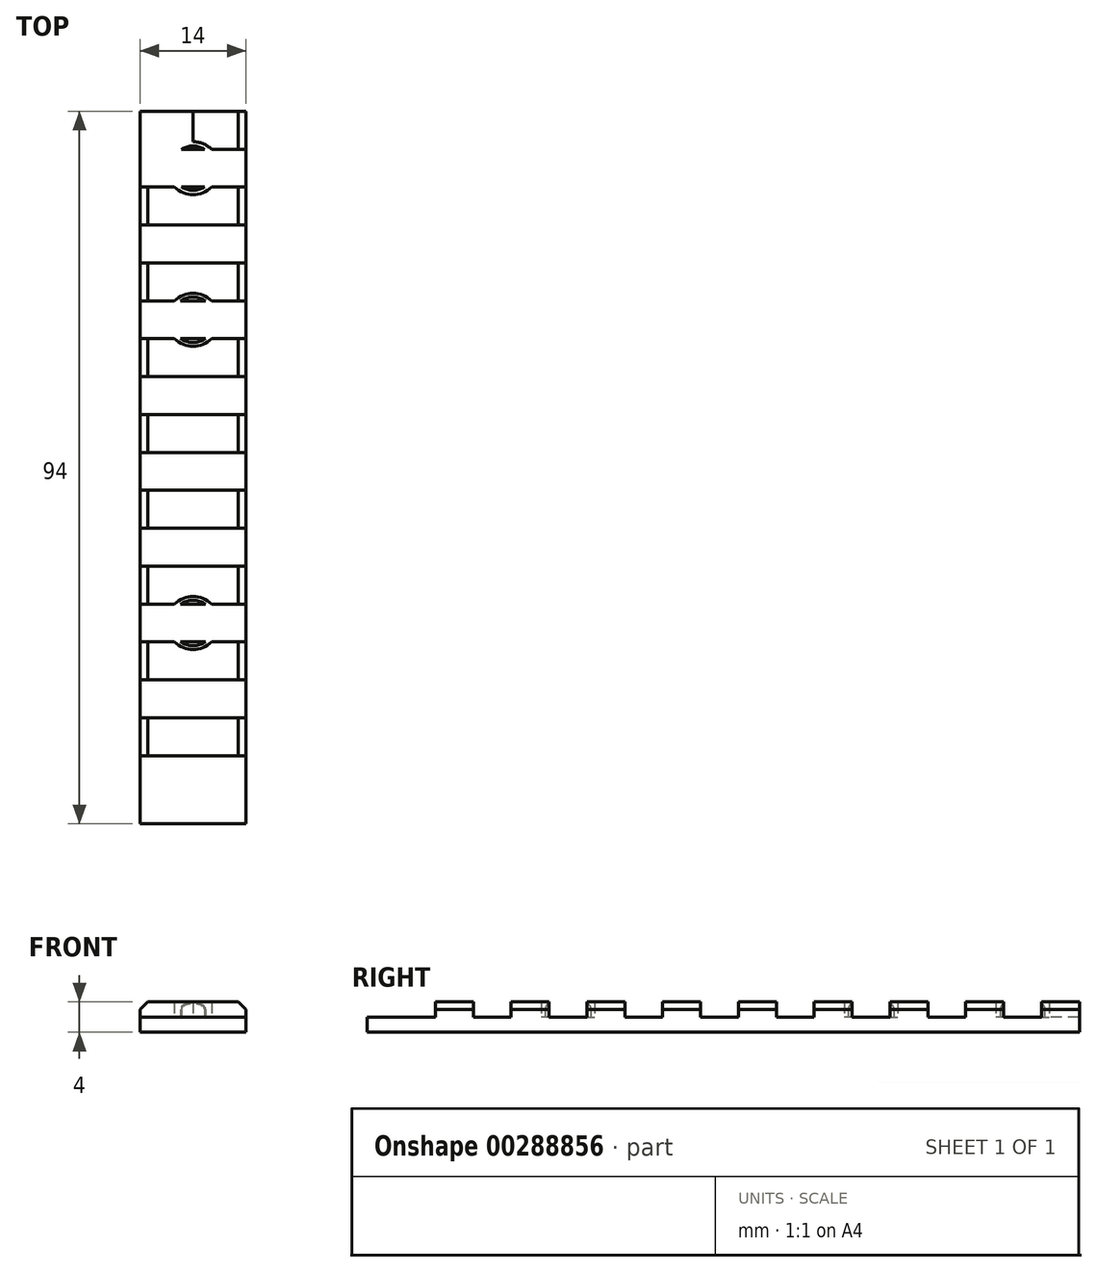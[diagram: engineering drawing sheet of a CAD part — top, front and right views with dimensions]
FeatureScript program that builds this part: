
annotation { "Feature Type Name" : "Feature", "Feature Type Description" : "" }
export const myFeature = defineFeature(function(context is Context, id is Id, definition is map)
    precondition{}
    {
        {
            var Q0;
            Q0=qCreatedBy(makeId("Top.planeOp"),FACE);
            var sketch = newSketch(context, id + "F0", { "sketchPlane" : qUnion([Q0])});
            skLineSegment(sketch, "E0.bottom", {"start": v(-14, 58.07) * mm, "end": v(0, 58.07) * mm});
            skLineSegment(sketch, "E0.top", {"start": v(-14, -35.93) * mm, "end": v(0, -35.93) * mm});
            skLineSegment(sketch, "E0.left", {"start": v(-14, 58.07) * mm, "end": v(-14, -35.93) * mm});
            skLineSegment(sketch, "E0.right", {"start": v(0, 58.07) * mm, "end": v(0, -35.93) * mm});
            skSolve(sketch);
        }
        {
            var Q0;
            Q0 = qSketchRegion(id + "F0", true);
            extrude(context, id + "F1", {"entities" : qUnion([Q0]), "depth" : 2 * mm});
        }
        {
            var Q0;
            Q0=makeQuery(id+"F1.opExtrude","CAP_FACE",FACE,{"disambiguationData":[OSD([sQuery(id+"F0.wireOp",EDGE,"E0.bottom"),sQuery(id+"F0.wireOp",EDGE,"E0.top"),sQuery(id+"F0.wireOp",EDGE,"E0.left"),sQuery(id+"F0.wireOp",EDGE,"E0.right")])],"isStart":false});
            var sketch = newSketch(context, id + "F2", { "sketchPlane" : qUnion([Q0])});
            skLineSegment(sketch, "E1", {"start": v(-14, 58.07) * mm, "end": v(-14, 48.07) * mm});
            skLineSegment(sketch, "E2.bottom", {"start": v(-14, 48.07) * mm, "end": v(0, 48.07) * mm});
            skLineSegment(sketch, "E2.top", {"start": v(-14, 43.07) * mm, "end": v(0, 43.07) * mm});
            skLineSegment(sketch, "E2.left", {"start": v(-14, 48.07) * mm, "end": v(-14, 43.07) * mm});
            skLineSegment(sketch, "E2.right", {"start": v(0, 48.07) * mm, "end": v(0, 43.07) * mm});
            skLineSegment(sketch, "E3", {"start": v(-14, 43.07) * mm, "end": v(-14, 38.07) * mm});
            skLineSegment(sketch, "E4.bottom", {"start": v(-14, 38.07) * mm, "end": v(0, 38.07) * mm});
            skLineSegment(sketch, "E4.top", {"start": v(-14, 33.07) * mm, "end": v(0, 33.07) * mm});
            skLineSegment(sketch, "E4.left", {"start": v(-14, 38.07) * mm, "end": v(-14, 33.07) * mm});
            skLineSegment(sketch, "E4.right", {"start": v(0, 38.07) * mm, "end": v(0, 33.07) * mm});
            skLineSegment(sketch, "E5", {"start": v(-14, 33.07) * mm, "end": v(-14, 28.07) * mm});
            skLineSegment(sketch, "E6.bottom", {"start": v(-14, 28.07) * mm, "end": v(0, 28.07) * mm});
            skLineSegment(sketch, "E6.top", {"start": v(-14, 23.07) * mm, "end": v(0, 23.07) * mm});
            skLineSegment(sketch, "E6.left", {"start": v(-14, 28.07) * mm, "end": v(-14, 23.07) * mm});
            skLineSegment(sketch, "E6.right", {"start": v(0, 28.07) * mm, "end": v(0, 23.07) * mm});
            skLineSegment(sketch, "E7", {"start": v(-14, 23.07) * mm, "end": v(-14, 18.07) * mm});
            skLineSegment(sketch, "E8.bottom", {"start": v(-14, 18.07) * mm, "end": v(0, 18.07) * mm});
            skLineSegment(sketch, "E8.top", {"start": v(-14, 13.07) * mm, "end": v(0, 13.07) * mm});
            skLineSegment(sketch, "E8.left", {"start": v(-14, 18.07) * mm, "end": v(-14, 13.07) * mm});
            skLineSegment(sketch, "E8.right", {"start": v(0, 18.07) * mm, "end": v(0, 13.07) * mm});
            skLineSegment(sketch, "E9", {"start": v(-14, 13.07) * mm, "end": v(-14, 8.07) * mm});
            skLineSegment(sketch, "E10.bottom", {"start": v(-14, 8.07) * mm, "end": v(0, 8.07) * mm});
            skLineSegment(sketch, "E10.top", {"start": v(-14, 3.07) * mm, "end": v(0, 3.07) * mm});
            skLineSegment(sketch, "E10.left", {"start": v(-14, 8.07) * mm, "end": v(-14, 3.07) * mm});
            skLineSegment(sketch, "E10.right", {"start": v(0, 8.07) * mm, "end": v(0, 3.07) * mm});
            skLineSegment(sketch, "E11", {"start": v(-14, 3.07) * mm, "end": v(-14, -1.93) * mm});
            skLineSegment(sketch, "E12.bottom", {"start": v(-14, -1.93) * mm, "end": v(0, -1.93) * mm});
            skLineSegment(sketch, "E12.top", {"start": v(-14, -6.93) * mm, "end": v(-9.45, -6.93) * mm});
            skLineSegment(sketch, "E12.left", {"start": v(-14, -1.93) * mm, "end": v(-14, -6.93) * mm});
            skLineSegment(sketch, "E12.right", {"start": v(0, -1.93) * mm, "end": v(0, -6.93) * mm});
            skLineSegment(sketch, "E13", {"start": v(-14, -6.93) * mm, "end": v(-14, -11.93) * mm});
            skLineSegment(sketch, "E14.bottom", {"start": v(-14, -11.93) * mm, "end": v(-9.45, -11.93) * mm});
            skLineSegment(sketch, "E14.top", {"start": v(-14, -16.93) * mm, "end": v(0, -16.93) * mm});
            skLineSegment(sketch, "E14.left", {"start": v(-14, -11.93) * mm, "end": v(-14, -16.93) * mm});
            skLineSegment(sketch, "E14.right", {"start": v(0, -11.93) * mm, "end": v(0, -16.93) * mm});
            skLineSegment(sketch, "E15", {"start": v(-14, -16.93) * mm, "end": v(-14, -21.93) * mm});
            skLineSegment(sketch, "E16.bottom", {"start": v(-14, -21.93) * mm, "end": v(0, -21.93) * mm});
            skLineSegment(sketch, "E16.top", {"start": v(-14, -26.93) * mm, "end": v(0, -26.93) * mm});
            skLineSegment(sketch, "E16.left", {"start": v(-14, -21.93) * mm, "end": v(-14, -26.93) * mm});
            skLineSegment(sketch, "E16.right", {"start": v(0, -21.93) * mm, "end": v(0, -26.93) * mm});
            skLineSegment(sketch, "E17.bottom", {"start": v(-14, 58.07) * mm, "end": v(0, 58.07) * mm});
            skLineSegment(sketch, "E17.top", {"start": v(-14, 53.07) * mm, "end": v(0, 53.07) * mm});
            skLineSegment(sketch, "E17.left", {"start": v(-14, 58.07) * mm, "end": v(-14, 53.07) * mm});
            skLineSegment(sketch, "E17.right", {"start": v(0, 58.07) * mm, "end": v(0, 53.07) * mm});
            skLineSegment(sketch, "E18", {"start": v(-7, 58.07) * mm, "end": v(-7, -35.93) * mm});
            skPoint(sketch, "E19", {"position": v(-7, 53.07) * mm});
            skPoint(sketch, "E20", {"position": v(-7, 48.07) * mm});
            skLineSegment(sketch, "E21", {"start": v(-7, 53.07) * mm, "end": v(-7, 48.07) * mm});
            skPoint(sketch, "E22", {"position": v(-7, 43.07) * mm});
            skPoint(sketch, "E23", {"position": v(-7, 38.07) * mm});
            skLineSegment(sketch, "E24", {"start": v(-7, 43.07) * mm, "end": v(-7, 38.07) * mm});
            skCircle(sketch, "E25", {"center": v(-7, 50.57) * mm, "radius": 3.5 * mm});
            skPoint(sketch, "E26", {"position": v(-7, 33.07) * mm});
            skPoint(sketch, "E27", {"position": v(-7, 28.07) * mm});
            skLineSegment(sketch, "E28", {"start": v(-7, 33.07) * mm, "end": v(-7, 28.07) * mm});
            skCircle(sketch, "E29", {"center": v(-7, 30.57) * mm, "radius": 3.5 * mm});
            skLineSegment(sketch, "E30", {"start": v(-7, -6.93) * mm, "end": v(-7, -11.93) * mm});
            skCircle(sketch, "E31", {"center": v(-7, -9.43) * mm, "radius": 3.5 * mm});
            skLineSegment(sketch, "E32", {"start": v(-9.45, -6.93) * mm, "end": v(-4.55, -6.93) * mm});
            skLineSegment(sketch, "E33", {"start": v(-4.55, -6.93) * mm, "end": v(0, -6.93) * mm});
            skLineSegment(sketch, "E34", {"start": v(-9.45, -11.93) * mm, "end": v(-4.55, -11.93) * mm});
            skLineSegment(sketch, "E35", {"start": v(-4.55, -11.93) * mm, "end": v(0, -11.93) * mm});
            skCircle(sketch, "E36", {"center": v(-7, -9.43) * mm, "radius": 3 * mm});
            skCircle(sketch, "E37", {"center": v(-7, 30.57) * mm, "radius": 3 * mm});
            skCircle(sketch, "E38", {"center": v(-7, 50.57) * mm, "radius": 2.92 * mm});
            skSolve(sketch);
        }
        {
            var Q0;
            {var subQ5=sQuery(id+"F2.wireOp",EDGE,"E17.left");Q0=makeQuery(id+"F2.imprint","IMPRINT",FACE,{"disambiguationData":[TD([[makeQuery(id+"F2.imprint","IMPRINT",EDGE,{"derivedFrom":subQ5}),1.0]])]});}
            var Q1;
            {var subQ7=sQuery(id+"F2.wireOp",EDGE,"E17.right");Q1=makeQuery(id+"F2.imprint","IMPRINT",FACE,{"disambiguationData":[TD([[makeQuery(id+"F2.imprint","IMPRINT",EDGE,{"derivedFrom":subQ7}),-1.0]])]});}
            var Q2;
            {var subQ0=sQuery(id+"F2.wireOp",EDGE,"E2.left");Q2=makeQuery(id+"F2.imprint","IMPRINT",FACE,{"disambiguationData":[TD([[makeQuery(id+"F2.imprint","IMPRINT",EDGE,{"derivedFrom":subQ0}),1.0]])]});}
            var Q3;
            {var subQ0=sQuery(id+"F2.wireOp",EDGE,"E2.right");Q3=makeQuery(id+"F2.imprint","IMPRINT",FACE,{"disambiguationData":[TD([[makeQuery(id+"F2.imprint","IMPRINT",EDGE,{"derivedFrom":subQ0}),-1.0]])]});}
            var Q4;
            {var subQ5=sQuery(id+"F2.wireOp",EDGE,"E4.right");Q4=makeQuery(id+"F2.imprint","IMPRINT",FACE,{"disambiguationData":[TD([[makeQuery(id+"F2.imprint","IMPRINT",EDGE,{"derivedFrom":subQ5}),-1.0]])]});}
            var Q5;
            {var subQ0=sQuery(id+"F2.wireOp",EDGE,"E4.left");Q5=makeQuery(id+"F2.imprint","IMPRINT",FACE,{"disambiguationData":[TD([[makeQuery(id+"F2.imprint","IMPRINT",EDGE,{"derivedFrom":subQ0}),1.0]])]});}
            var Q6;
            {var subQ5=sQuery(id+"F2.wireOp",EDGE,"E6.left");Q6=makeQuery(id+"F2.imprint","IMPRINT",FACE,{"disambiguationData":[TD([[makeQuery(id+"F2.imprint","IMPRINT",EDGE,{"derivedFrom":subQ5}),1.0]])]});}
            var Q7;
            {var subQ5=sQuery(id+"F2.wireOp",EDGE,"E6.right");Q7=makeQuery(id+"F2.imprint","IMPRINT",FACE,{"disambiguationData":[TD([[makeQuery(id+"F2.imprint","IMPRINT",EDGE,{"derivedFrom":subQ5}),-1.0]])]});}
            var Q8;
            {var subQ0=sQuery(id+"F2.wireOp",EDGE,"E8.left");Q8=makeQuery(id+"F2.imprint","IMPRINT",FACE,{"disambiguationData":[TD([[makeQuery(id+"F2.imprint","IMPRINT",EDGE,{"derivedFrom":subQ0}),1.0]])]});}
            var Q9;
            {var subQ0=sQuery(id+"F2.wireOp",EDGE,"E8.right");Q9=makeQuery(id+"F2.imprint","IMPRINT",FACE,{"disambiguationData":[TD([[makeQuery(id+"F2.imprint","IMPRINT",EDGE,{"derivedFrom":subQ0}),-1.0]])]});}
            var Q10;
            {var subQ0=sQuery(id+"F2.wireOp",EDGE,"E10.left");Q10=makeQuery(id+"F2.imprint","IMPRINT",FACE,{"disambiguationData":[TD([[makeQuery(id+"F2.imprint","IMPRINT",EDGE,{"derivedFrom":subQ0}),1.0]])]});}
            var Q11;
            {var subQ0=sQuery(id+"F2.wireOp",EDGE,"E10.right");Q11=makeQuery(id+"F2.imprint","IMPRINT",FACE,{"disambiguationData":[TD([[makeQuery(id+"F2.imprint","IMPRINT",EDGE,{"derivedFrom":subQ0}),-1.0]])]});}
            var Q12;
            {var subQ6=sQuery(id+"F2.wireOp",EDGE,"E12.top");Q12=makeQuery(id+"F2.imprint","IMPRINT",FACE,{"disambiguationData":[TD([[makeQuery(id+"F2.imprint","IMPRINT",EDGE,{"derivedFrom":subQ6}),1.0]])]});}
            var Q13;
            {var subQ6=sQuery(id+"F2.wireOp",EDGE,"E12.right");Q13=makeQuery(id+"F2.imprint","IMPRINT",FACE,{"disambiguationData":[TD([[makeQuery(id+"F2.imprint","IMPRINT",EDGE,{"derivedFrom":subQ6}),-1.0]])]});}
            var Q14;
            {var subQ6=sQuery(id+"F2.wireOp",EDGE,"E14.bottom");Q14=makeQuery(id+"F2.imprint","IMPRINT",FACE,{"disambiguationData":[TD([[makeQuery(id+"F2.imprint","IMPRINT",EDGE,{"derivedFrom":subQ6}),-1.0]])]});}
            var Q15;
            {var subQ6=sQuery(id+"F2.wireOp",EDGE,"E14.right");Q15=makeQuery(id+"F2.imprint","IMPRINT",FACE,{"disambiguationData":[TD([[makeQuery(id+"F2.imprint","IMPRINT",EDGE,{"derivedFrom":subQ6}),-1.0]])]});}
            var Q16;
            {var subQ0=sQuery(id+"F2.wireOp",EDGE,"E16.left");Q16=makeQuery(id+"F2.imprint","IMPRINT",FACE,{"disambiguationData":[TD([[makeQuery(id+"F2.imprint","IMPRINT",EDGE,{"derivedFrom":subQ0}),1.0]])]});}
            var Q17;
            {var subQ0=sQuery(id+"F2.wireOp",EDGE,"E16.right");Q17=makeQuery(id+"F2.imprint","IMPRINT",FACE,{"disambiguationData":[TD([[makeQuery(id+"F2.imprint","IMPRINT",EDGE,{"derivedFrom":subQ0}),-1.0]])]});}
            var Q18;
            {var subQ0=sQuery(id+"F2.wireOp",EDGE,"E21");Q18=makeQuery(id+"F2.imprint","IMPRINT",FACE,{"disambiguationData":[TD([[makeQuery(id+"F2.imprint","IMPRINT",EDGE,{"derivedFrom":subQ0}),-1.0]])]});}
            var Q19;
            {var subQ0=sQuery(id+"F2.wireOp",EDGE,"E21");Q19=makeQuery(id+"F2.imprint","IMPRINT",FACE,{"disambiguationData":[TD([[makeQuery(id+"F2.imprint","IMPRINT",EDGE,{"derivedFrom":subQ0}),1.0]])]});}
            var Q20;
            {var subQ1=sQuery(id+"F2.wireOp",EDGE,"E17.top");var subQ3=sQuery(id+"F2.wireOp",EDGE,"E38");var subQ4=makeQuery(id+"F2.imprint","INTERSECT",VERTEX,{"disambiguationData":[OD(1.0)],"derivedFrom":[subQ1,subQ3]});Q20=makeQuery(id+"F2.imprint","IMPRINT",FACE,{"disambiguationData":[TD([[makeQuery(id+"F2.imprint","IMPRINT",EDGE,{"disambiguationData":[TD([[subQ4,-1.0]])],"derivedFrom":subQ3}),1.0]])]});}
            var Q21;
            {var subQ1=sQuery(id+"F2.wireOp",EDGE,"E17.top");var subQ3=sQuery(id+"F2.wireOp",EDGE,"E38");var subQ4=makeQuery(id+"F2.imprint","INTERSECT",VERTEX,{"disambiguationData":[OD(0.0)],"derivedFrom":[subQ1,subQ3]});Q21=makeQuery(id+"F2.imprint","IMPRINT",FACE,{"disambiguationData":[TD([[makeQuery(id+"F2.imprint","IMPRINT",EDGE,{"disambiguationData":[TD([[subQ4,1.0]])],"derivedFrom":subQ3}),1.0]])]});}
            var Q22;
            {var subQ1=sQuery(id+"F2.wireOp",EDGE,"E2.bottom");var subQ3=sQuery(id+"F2.wireOp",EDGE,"E38");var subQ4=makeQuery(id+"F2.imprint","INTERSECT",VERTEX,{"disambiguationData":[OD(0.0)],"derivedFrom":[subQ1,subQ3]});Q22=makeQuery(id+"F2.imprint","IMPRINT",FACE,{"disambiguationData":[TD([[makeQuery(id+"F2.imprint","IMPRINT",EDGE,{"disambiguationData":[TD([[subQ4,-1.0]])],"derivedFrom":subQ3}),1.0]])]});}
            var Q23;
            {var subQ1=sQuery(id+"F2.wireOp",EDGE,"E2.bottom");var subQ3=sQuery(id+"F2.wireOp",EDGE,"E38");var subQ4=makeQuery(id+"F2.imprint","INTERSECT",VERTEX,{"disambiguationData":[OD(1.0)],"derivedFrom":[subQ1,subQ3]});Q23=makeQuery(id+"F2.imprint","IMPRINT",FACE,{"disambiguationData":[TD([[makeQuery(id+"F2.imprint","IMPRINT",EDGE,{"disambiguationData":[TD([[subQ4,1.0]])],"derivedFrom":subQ3}),1.0]])]});}
            var Q24;
            {var subQ1=sQuery(id+"F2.wireOp",EDGE,"E4.top");var subQ3=sQuery(id+"F2.wireOp",EDGE,"E37");var subQ4=makeQuery(id+"F2.imprint","INTERSECT",VERTEX,{"disambiguationData":[OD(0.0)],"derivedFrom":[subQ1,subQ3]});Q24=makeQuery(id+"F2.imprint","IMPRINT",FACE,{"disambiguationData":[TD([[makeQuery(id+"F2.imprint","IMPRINT",EDGE,{"disambiguationData":[TD([[subQ4,1.0]])],"derivedFrom":subQ3}),1.0]])]});}
            var Q25;
            {var subQ1=sQuery(id+"F2.wireOp",EDGE,"E4.top");var subQ3=sQuery(id+"F2.wireOp",EDGE,"E37");var subQ4=makeQuery(id+"F2.imprint","INTERSECT",VERTEX,{"disambiguationData":[OD(1.0)],"derivedFrom":[subQ1,subQ3]});Q25=makeQuery(id+"F2.imprint","IMPRINT",FACE,{"disambiguationData":[TD([[makeQuery(id+"F2.imprint","IMPRINT",EDGE,{"disambiguationData":[TD([[subQ4,-1.0]])],"derivedFrom":subQ3}),1.0]])]});}
            var Q26;
            {var subQ0=sQuery(id+"F2.wireOp",EDGE,"E28");Q26=makeQuery(id+"F2.imprint","IMPRINT",FACE,{"disambiguationData":[TD([[makeQuery(id+"F2.imprint","IMPRINT",EDGE,{"derivedFrom":subQ0}),1.0]])]});}
            var Q27;
            {var subQ0=sQuery(id+"F2.wireOp",EDGE,"E28");Q27=makeQuery(id+"F2.imprint","IMPRINT",FACE,{"disambiguationData":[TD([[makeQuery(id+"F2.imprint","IMPRINT",EDGE,{"derivedFrom":subQ0}),-1.0]])]});}
            var Q28;
            {var subQ1=sQuery(id+"F2.wireOp",EDGE,"E6.bottom");var subQ3=sQuery(id+"F2.wireOp",EDGE,"E37");var subQ4=makeQuery(id+"F2.imprint","INTERSECT",VERTEX,{"disambiguationData":[OD(0.0)],"derivedFrom":[subQ1,subQ3]});Q28=makeQuery(id+"F2.imprint","IMPRINT",FACE,{"disambiguationData":[TD([[makeQuery(id+"F2.imprint","IMPRINT",EDGE,{"disambiguationData":[TD([[subQ4,-1.0]])],"derivedFrom":subQ3}),1.0]])]});}
            var Q29;
            {var subQ1=sQuery(id+"F2.wireOp",EDGE,"E6.bottom");var subQ3=sQuery(id+"F2.wireOp",EDGE,"E37");var subQ4=makeQuery(id+"F2.imprint","INTERSECT",VERTEX,{"disambiguationData":[OD(1.0)],"derivedFrom":[subQ1,subQ3]});Q29=makeQuery(id+"F2.imprint","IMPRINT",FACE,{"disambiguationData":[TD([[makeQuery(id+"F2.imprint","IMPRINT",EDGE,{"disambiguationData":[TD([[subQ4,1.0]])],"derivedFrom":subQ3}),1.0]])]});}
            var Q30;
            {var subQ1=sQuery(id+"F2.wireOp",EDGE,"E18");var subQ3=sQuery(id+"F2.wireOp",EDGE,"E36");var subQ4=makeQuery(id+"F2.imprint","INTERSECT",VERTEX,{"disambiguationData":[OD(0.0)],"derivedFrom":[subQ1,subQ3]});Q30=makeQuery(id+"F2.imprint","IMPRINT",FACE,{"disambiguationData":[TD([[makeQuery(id+"F2.imprint","IMPRINT",EDGE,{"disambiguationData":[TD([[subQ4,-1.0]])],"derivedFrom":subQ3}),1.0]])]});}
            var Q31;
            {var subQ1=sQuery(id+"F2.wireOp",EDGE,"E18");var subQ3=sQuery(id+"F2.wireOp",EDGE,"E36");var subQ4=makeQuery(id+"F2.imprint","INTERSECT",VERTEX,{"disambiguationData":[OD(0.0)],"derivedFrom":[subQ1,subQ3]});Q31=makeQuery(id+"F2.imprint","IMPRINT",FACE,{"disambiguationData":[TD([[makeQuery(id+"F2.imprint","IMPRINT",EDGE,{"disambiguationData":[TD([[subQ4,1.0]])],"derivedFrom":subQ3}),1.0]])]});}
            var Q32;
            {var subQ0=sQuery(id+"F2.wireOp",EDGE,"E30");Q32=makeQuery(id+"F2.imprint","IMPRINT",FACE,{"disambiguationData":[TD([[makeQuery(id+"F2.imprint","IMPRINT",EDGE,{"derivedFrom":subQ0}),1.0]])]});}
            var Q33;
            {var subQ0=sQuery(id+"F2.wireOp",EDGE,"E30");Q33=makeQuery(id+"F2.imprint","IMPRINT",FACE,{"disambiguationData":[TD([[makeQuery(id+"F2.imprint","IMPRINT",EDGE,{"derivedFrom":subQ0}),-1.0]])]});}
            var Q34;
            {var subQ1=sQuery(id+"F2.wireOp",EDGE,"E18");var subQ3=sQuery(id+"F2.wireOp",EDGE,"E36");var subQ4=makeQuery(id+"F2.imprint","INTERSECT",VERTEX,{"disambiguationData":[OD(1.0)],"derivedFrom":[subQ1,subQ3]});Q34=makeQuery(id+"F2.imprint","IMPRINT",FACE,{"disambiguationData":[TD([[makeQuery(id+"F2.imprint","IMPRINT",EDGE,{"disambiguationData":[TD([[subQ4,1.0]])],"derivedFrom":subQ3}),1.0]])]});}
            var Q35;
            {var subQ1=sQuery(id+"F2.wireOp",EDGE,"E18");var subQ3=sQuery(id+"F2.wireOp",EDGE,"E36");var subQ4=makeQuery(id+"F2.imprint","INTERSECT",VERTEX,{"disambiguationData":[OD(1.0)],"derivedFrom":[subQ1,subQ3]});Q35=makeQuery(id+"F2.imprint","IMPRINT",FACE,{"disambiguationData":[TD([[makeQuery(id+"F2.imprint","IMPRINT",EDGE,{"disambiguationData":[TD([[subQ4,-1.0]])],"derivedFrom":subQ3}),1.0]])]});}
            extrude(context, id + "F3", {"entities" : qUnion([Q0, Q1, Q2, Q3, Q4, Q5, Q6, Q7, Q8, Q9, Q10, Q11, Q12, Q13, Q14, Q15, Q16, Q17, Q18, Q19, Q20, Q21, Q22, Q23, Q24, Q25, Q26, Q27, Q28, Q29, Q30, Q31, Q32, Q33, Q34, Q35]), "operationType" : NewBodyOperationType.ADD, "depth" : 2 * mm});
        }
        {
            var Q0;
            Q0=makeQuery(id+"F3.opExtrude","CAP_EDGE",EDGE,{"disambiguationData":[OSD([sQuery(id+"F2.wireOp",EDGE,"E17.left")])],"isStart":false});
            var Q1;
            Q1=makeQuery(id+"F3.opExtrude","CAP_EDGE",EDGE,{"disambiguationData":[OSD([sQuery(id+"F2.wireOp",EDGE,"E2.left")])],"isStart":false});
            var Q2;
            Q2=makeQuery(id+"F3.opExtrude","CAP_EDGE",EDGE,{"disambiguationData":[OSD([sQuery(id+"F2.wireOp",EDGE,"E4.left")])],"isStart":false});
            var Q3;
            Q3=makeQuery(id+"F3.opExtrude","CAP_EDGE",EDGE,{"disambiguationData":[OSD([sQuery(id+"F2.wireOp",EDGE,"E6.left")])],"isStart":false});
            var Q4;
            Q4=makeQuery(id+"F3.opExtrude","CAP_EDGE",EDGE,{"disambiguationData":[OSD([sQuery(id+"F2.wireOp",EDGE,"E8.left")])],"isStart":false});
            var Q5;
            Q5=makeQuery(id+"F3.opExtrude","CAP_EDGE",EDGE,{"disambiguationData":[OSD([sQuery(id+"F2.wireOp",EDGE,"E10.left")])],"isStart":false});
            var Q6;
            Q6=makeQuery(id+"F3.opExtrude","CAP_EDGE",EDGE,{"disambiguationData":[OSD([sQuery(id+"F2.wireOp",EDGE,"E12.left")])],"isStart":false});
            var Q7;
            Q7=makeQuery(id+"F3.opExtrude","CAP_EDGE",EDGE,{"disambiguationData":[OSD([sQuery(id+"F2.wireOp",EDGE,"E14.left")])],"isStart":false});
            var Q8;
            Q8=makeQuery(id+"F3.opExtrude","CAP_EDGE",EDGE,{"disambiguationData":[OSD([sQuery(id+"F2.wireOp",EDGE,"E16.left")])],"isStart":false});
            var Q9;
            Q9=makeQuery(id+"F3.opExtrude","CAP_EDGE",EDGE,{"disambiguationData":[OSD([sQuery(id+"F2.wireOp",EDGE,"E16.right")])],"isStart":false});
            var Q10;
            Q10=makeQuery(id+"F3.opExtrude","CAP_EDGE",EDGE,{"disambiguationData":[OSD([sQuery(id+"F2.wireOp",EDGE,"E14.right")])],"isStart":false});
            var Q11;
            Q11=makeQuery(id+"F3.opExtrude","CAP_EDGE",EDGE,{"disambiguationData":[OSD([sQuery(id+"F2.wireOp",EDGE,"E12.right")])],"isStart":false});
            var Q12;
            Q12=makeQuery(id+"F3.opExtrude","CAP_EDGE",EDGE,{"disambiguationData":[OSD([sQuery(id+"F2.wireOp",EDGE,"E10.right")])],"isStart":false});
            var Q13;
            Q13=makeQuery(id+"F3.opExtrude","CAP_EDGE",EDGE,{"disambiguationData":[OSD([sQuery(id+"F2.wireOp",EDGE,"E8.right")])],"isStart":false});
            var Q14;
            Q14=makeQuery(id+"F3.opExtrude","CAP_EDGE",EDGE,{"disambiguationData":[OSD([sQuery(id+"F2.wireOp",EDGE,"E6.right")])],"isStart":false});
            var Q15;
            Q15=makeQuery(id+"F3.opExtrude","CAP_EDGE",EDGE,{"disambiguationData":[OSD([sQuery(id+"F2.wireOp",EDGE,"E4.right")])],"isStart":false});
            var Q16;
            Q16=makeQuery(id+"F3.opExtrude","CAP_EDGE",EDGE,{"disambiguationData":[OSD([sQuery(id+"F2.wireOp",EDGE,"E2.right")])],"isStart":false});
            var Q17;
            Q17=makeQuery(id+"F3.opExtrude","CAP_EDGE",EDGE,{"disambiguationData":[OSD([sQuery(id+"F2.wireOp",EDGE,"E17.right")])],"isStart":false});
            chamfer(context, id + "F4", {"entities" : qUnion([Q0, Q1, Q2, Q3, Q4, Q5, Q6, Q7, Q8, Q9, Q10, Q11, Q12, Q13, Q14, Q15, Q16, Q17]), "width" : 1 * mm, "tangentPropagation" : true});
        }
        {
            var Q0;
            Q0=makeQuery(id+"F3.opExtrude","CAP_EDGE",EDGE,{"disambiguationData":[OSD([sQuery(id+"F2.wireOp",EDGE,"E36")])],"isStart":false});
            var Q1;
            Q1=makeQuery(id+"F3.opExtrude","CAP_EDGE",EDGE,{"disambiguationData":[OSD([sQuery(id+"F2.wireOp",EDGE,"E37")])],"isStart":false});
            var Q2;
            Q2=makeQuery(id+"F3.opExtrude","CAP_EDGE",EDGE,{"disambiguationData":[OSD([sQuery(id+"F2.wireOp",EDGE,"E38")])],"isStart":false});
            fillet(context, id + "F5", {"entities" : qUnion([Q0, Q1, Q2]), "radius" : 1 * mm, "tangentPropagation" : true, "allowEdgeOverflow" : false});
        }
    });
